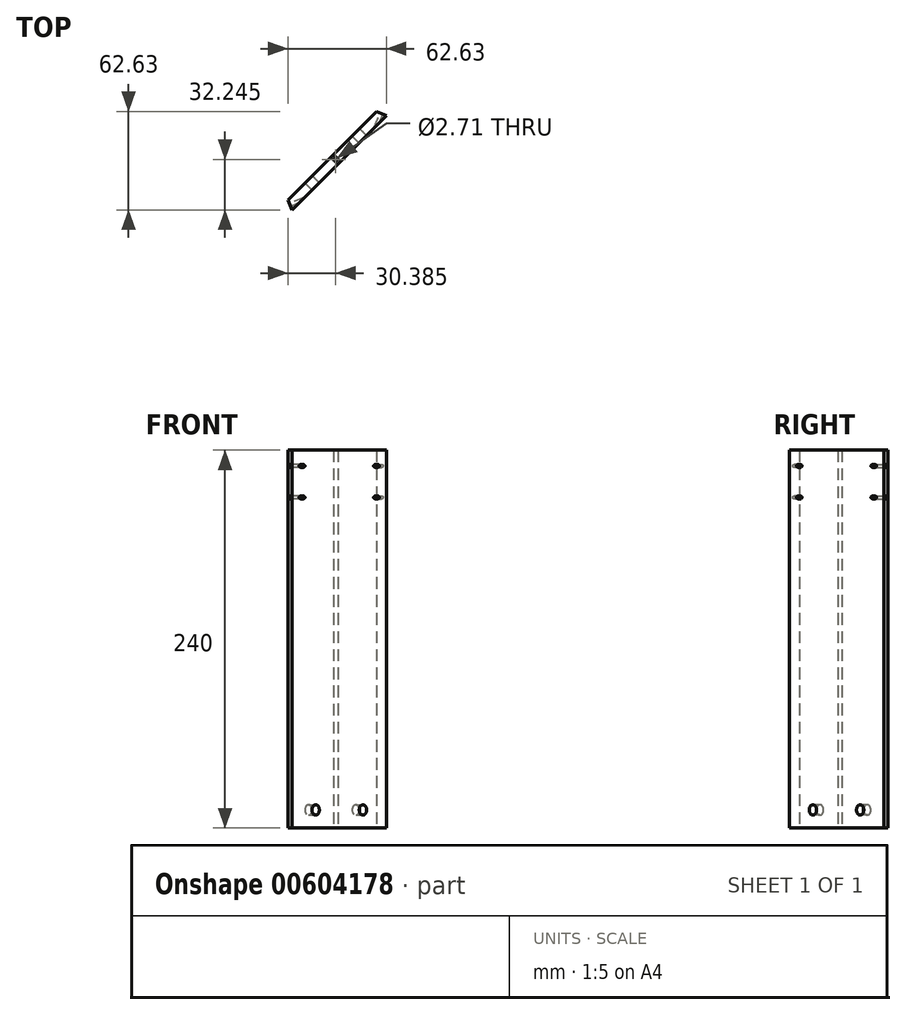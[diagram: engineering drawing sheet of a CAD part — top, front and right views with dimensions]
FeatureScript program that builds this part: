
annotation { "Feature Type Name" : "Feature", "Feature Type Description" : "" }
export const myFeature = defineFeature(function(context is Context, id is Id, definition is map)
    precondition{}
    {
        {
            var Q0;
            Q0=qCreatedBy(makeId("Top.planeOp"),FACE);
            var sketch = newSketch(context, id + "F0", { "sketchPlane" : qUnion([Q0])});
            skLineSegment(sketch, "E0", {"start": v(-120, 0) * mm, "end": v(-180, 60) * mm});
            skLineSegment(sketch, "E1", {"start": v(-180, 60) * mm, "end": v(-180, 220) * mm});
            skLineSegment(sketch, "E2", {"start": v(-180, 220) * mm, "end": v(-120, 280) * mm});
            skLineSegment(sketch, "E3", {"start": v(-120, 280) * mm, "end": v(120, 280) * mm});
            skLineSegment(sketch, "E4", {"start": v(120, 280) * mm, "end": v(180, 220) * mm});
            skLineSegment(sketch, "E5", {"start": v(180, 220) * mm, "end": v(180, 60) * mm});
            skLineSegment(sketch, "E6", {"start": v(180, 60) * mm, "end": v(120, 0) * mm});
            skLineSegment(sketch, "E7", {"start": v(120, 0) * mm, "end": v(-120, 0) * mm});
            skLineSegment(sketch, "E8.0", {"start": v(-173.65, 62.63) * mm, "end": v(-173.65, 217.37) * mm});
            skLineSegment(sketch, "E8.1", {"start": v(-117.37, 6.35) * mm, "end": v(-173.65, 62.63) * mm});
            skLineSegment(sketch, "E8.2", {"start": v(-173.65, 217.37) * mm, "end": v(-117.37, 273.65) * mm});
            skLineSegment(sketch, "E8.3", {"start": v(117.37, 6.35) * mm, "end": v(-117.37, 6.35) * mm});
            skLineSegment(sketch, "E8.4", {"start": v(-117.37, 273.65) * mm, "end": v(117.37, 273.65) * mm});
            skLineSegment(sketch, "E8.5", {"start": v(117.37, 273.65) * mm, "end": v(173.65, 217.37) * mm});
            skLineSegment(sketch, "E8.6", {"start": v(173.65, 217.37) * mm, "end": v(173.65, 62.63) * mm});
            skLineSegment(sketch, "E8.7", {"start": v(173.65, 62.63) * mm, "end": v(117.37, 6.35) * mm});
            skLineSegment(sketch, "E9", {"start": v(-120, 0) * mm, "end": v(-117.37, 6.35) * mm});
            skLineSegment(sketch, "E10", {"start": v(-120, 280) * mm, "end": v(-117.37, 273.65) * mm});
            skLineSegment(sketch, "E11", {"start": v(120, 280) * mm, "end": v(117.37, 273.65) * mm});
            skLineSegment(sketch, "E12", {"start": v(120, 0) * mm, "end": v(117.37, 6.35) * mm});
            skLineSegment(sketch, "E13", {"start": v(-173.65, 217.37) * mm, "end": v(-180, 220) * mm});
            skLineSegment(sketch, "E14", {"start": v(-173.65, 62.63) * mm, "end": v(-180, 60) * mm});
            skLineSegment(sketch, "E15", {"start": v(173.65, 62.63) * mm, "end": v(180, 60) * mm});
            skLineSegment(sketch, "E16", {"start": v(173.65, 217.37) * mm, "end": v(180, 220) * mm});
            skSolve(sketch);
        }
        {
            var Q0;
            Q0=makeQuery(id+"F0.imprint","IMPRINT",FACE,{"disambiguationData":[TD([[makeQuery(id+"F0.imprint","IMPRINT",EDGE,{"derivedFrom":sQuery(id+"F0.wireOp",EDGE,"E0")}),-1.0]])]});
            extrude(context, id + "F1", {"entities" : qUnion([Q0]), "depth" : 240 * mm, "offsetDistance" : 25 * mm});
        }
        {
            var Q0;
            Q0=makeQuery(id+"F0.imprint","IMPRINT",FACE,{"disambiguationData":[TD([[makeQuery(id+"F0.imprint","IMPRINT",EDGE,{"derivedFrom":sQuery(id+"F0.wireOp",EDGE,"E2")}),-1.0]])]});
            extrude(context, id + "F2", {"entities" : qUnion([Q0]), "depth" : 240 * mm, "offsetDistance" : 25 * mm});
        }
        {
            var Q0;
            Q0=makeQuery(id+"F0.imprint","IMPRINT",FACE,{"disambiguationData":[TD([[makeQuery(id+"F0.imprint","IMPRINT",EDGE,{"derivedFrom":sQuery(id+"F0.wireOp",EDGE,"E4")}),-1.0]])]});
            extrude(context, id + "F3", {"entities" : qUnion([Q0]), "depth" : 240 * mm, "offsetDistance" : 25 * mm});
        }
        {
            var Q0;
            Q0=makeQuery(id+"F0.imprint","IMPRINT",FACE,{"disambiguationData":[TD([[makeQuery(id+"F0.imprint","IMPRINT",EDGE,{"derivedFrom":sQuery(id+"F0.wireOp",EDGE,"E6")}),-1.0]])]});
            extrude(context, id + "F4", {"entities" : qUnion([Q0]), "depth" : 240 * mm, "offsetDistance" : 25 * mm});
        }
        {
            var Q0;
            Q0=makeQuery(id+"F1.opExtrude","SWEPT_FACE",FACE,{"disambiguationData":[OSD([sQuery(id+"F0.wireOp",EDGE,"E0")])]});
            var sketch = newSketch(context, id + "F5", { "sketchPlane" : qUnion([Q0])});
            skLineSegment(sketch, "E17", {"start": v(-169.7, 0) * mm, "end": v(-84.85, 0) * mm, "construction": true});
            skLineSegment(sketch, "E18", {"start": v(-84.85, 0) * mm, "end": v(-127.28, 0) * mm, "construction": true});
            skLineSegment(sketch, "E19", {"start": v(-127.28, 0) * mm, "end": v(-106.07, 0) * mm, "construction": true});
            skLineSegment(sketch, "E20", {"start": v(-106.07, 0) * mm, "end": v(-106.07, 11.51) * mm, "construction": true});
            skLineSegment(sketch, "E21", {"start": v(-127.28, 0) * mm, "end": v(-169.7, 0) * mm, "construction": true});
            skLineSegment(sketch, "E22", {"start": v(-148.5, 0) * mm, "end": v(-148.5, 11.51) * mm, "construction": true});
            skSolve(sketch);
        }
        {
            var Q0;
            Q0=makeQuery(id+"F4.opExtrude","SWEPT_FACE",FACE,{"disambiguationData":[OSD([sQuery(id+"F0.wireOp",EDGE,"E6")])]});
            var sketch = newSketch(context, id + "F6", { "sketchPlane" : qUnion([Q0])});
            skLineSegment(sketch, "E23", {"start": v(84.85, 0) * mm, "end": v(169.7, 0) * mm, "construction": true});
            skLineSegment(sketch, "E24", {"start": v(169.7, 0) * mm, "end": v(127.28, 0) * mm, "construction": true});
            skLineSegment(sketch, "E25", {"start": v(127.28, 0) * mm, "end": v(148.5, 0) * mm, "construction": true});
            skLineSegment(sketch, "E26", {"start": v(148.5, 0) * mm, "end": v(148.5, 11.51) * mm, "construction": true});
            skLineSegment(sketch, "E27", {"start": v(84.85, 0) * mm, "end": v(127.28, 0) * mm, "construction": true});
            skLineSegment(sketch, "E28", {"start": v(106.07, 0) * mm, "end": v(106.07, 11.51) * mm, "construction": true});
            skSolve(sketch);
        }
        {
            var Q0;
            Q0=makeQuery(id+"F3.opExtrude","SWEPT_FACE",FACE,{"disambiguationData":[OSD([sQuery(id+"F0.wireOp",EDGE,"E4")])]});
            var sketch = newSketch(context, id + "F7", { "sketchPlane" : qUnion([Q0])});
            skLineSegment(sketch, "E29", {"start": v(28.28, 0) * mm, "end": v(113.14, 0) * mm, "construction": true});
            skLineSegment(sketch, "E30", {"start": v(113.14, 0) * mm, "end": v(70.71, 0) * mm, "construction": true});
            skLineSegment(sketch, "E31", {"start": v(70.71, 0) * mm, "end": v(91.92, 0) * mm, "construction": true});
            skLineSegment(sketch, "E32", {"start": v(91.92, 0) * mm, "end": v(91.92, 11.51) * mm, "construction": true});
            skLineSegment(sketch, "E33", {"start": v(28.28, 0) * mm, "end": v(70.71, 0) * mm, "construction": true});
            skLineSegment(sketch, "E34", {"start": v(49.5, 0) * mm, "end": v(49.5, 11.51) * mm, "construction": true});
            skSolve(sketch);
        }
        {
            var Q0;
            Q0=makeQuery(id+"F2.opExtrude","SWEPT_FACE",FACE,{"disambiguationData":[OSD([sQuery(id+"F0.wireOp",EDGE,"E2")])]});
            var sketch = newSketch(context, id + "F8", { "sketchPlane" : qUnion([Q0])});
            skLineSegment(sketch, "E35", {"start": v(-113.14, 0) * mm, "end": v(-28.28, 0) * mm, "construction": true});
            skLineSegment(sketch, "E36", {"start": v(-28.28, 0) * mm, "end": v(-70.71, 0) * mm, "construction": true});
            skLineSegment(sketch, "E37", {"start": v(-70.71, 0) * mm, "end": v(-49.5, 0) * mm, "construction": true});
            skLineSegment(sketch, "E38", {"start": v(-49.5, 0) * mm, "end": v(-49.5, 11.51) * mm, "construction": true});
            skLineSegment(sketch, "E39", {"start": v(-113.14, 0) * mm, "end": v(-70.71, 0) * mm, "construction": true});
            skLineSegment(sketch, "E40", {"start": v(-91.92, 0) * mm, "end": v(-91.92, 11.51) * mm, "construction": true});
            skSolve(sketch);
        }
        {
            var Q0;
            Q0=sQuery(id+"F8.wireOp",VERTEX,"E40.end");
            var Q1;
            Q1=sQuery(id+"F8.wireOp",VERTEX,"E38.end");
            var Q2;
            Q2=sQuery(id+"F5.wireOp",VERTEX,"E20.end");
            var Q3;
            Q3=sQuery(id+"F5.wireOp",VERTEX,"E22.end");
            var Q4;
            Q4=sQuery(id+"F6.wireOp",VERTEX,"E26.end");
            var Q5;
            Q5=sQuery(id+"F6.wireOp",VERTEX,"E28.end");
            var Q6;
            Q6=sQuery(id+"F7.wireOp",VERTEX,"E34.end");
            var Q7;
            Q7=sQuery(id+"F7.wireOp",VERTEX,"E32.end");
            var Q8;
            Q8=makeQuery(id+"F2.opExtrude","SWEPT_BODY",BODY,{"disambiguationData":[OSD([sQuery(id+"F0.wireOp",EDGE,"E2"),sQuery(id+"F0.wireOp",EDGE,"E8.2"),sQuery(id+"F0.wireOp",EDGE,"E10"),sQuery(id+"F0.wireOp",EDGE,"E13")])]});
            var Q9;
            Q9=makeQuery(id+"F1.opExtrude","SWEPT_BODY",BODY,{"disambiguationData":[OSD([sQuery(id+"F0.wireOp",EDGE,"E0"),sQuery(id+"F0.wireOp",EDGE,"E8.1"),sQuery(id+"F0.wireOp",EDGE,"E9"),sQuery(id+"F0.wireOp",EDGE,"E14")])]});
            var Q10;
            Q10=makeQuery(id+"F4.opExtrude","SWEPT_BODY",BODY,{"disambiguationData":[OSD([sQuery(id+"F0.wireOp",EDGE,"E6"),sQuery(id+"F0.wireOp",EDGE,"E8.7"),sQuery(id+"F0.wireOp",EDGE,"E12"),sQuery(id+"F0.wireOp",EDGE,"E15")])]});
            var Q11;
            Q11=makeQuery(id+"F3.opExtrude","SWEPT_BODY",BODY,{"disambiguationData":[OSD([sQuery(id+"F0.wireOp",EDGE,"E4"),sQuery(id+"F0.wireOp",EDGE,"E8.5"),sQuery(id+"F0.wireOp",EDGE,"E11"),sQuery(id+"F0.wireOp",EDGE,"E16")])]});
            hole(context, id + "F9", {"style" : HoleStyle.SIMPLE, "endStyle" : HoleEndStyle.BLIND, "standardTappedOrClearance" : lookupTablePath({ "standard" : "ISO", "fit" : "Normal", "size" : "M6", "type" : "Clearance" }), "standardBlindInLast" : lookupTablePath({ "fit" : "Standard", "standard" : "ISO", "size" : "M6", "type" : "Clearance" }), "holeDiameter" : 6.6 * mm, "majorDiameter" : 5 * mm, "holeDepth" : 12 * mm, "isTappedThrough" : true, "tappedDepth" : 12 * mm, "tapClearance" : 3, "locations" : qUnion([Q0, Q1, Q2, Q3, Q4, Q5, Q6, Q7]), "scope" : qUnion([Q8, Q9, Q10, Q11])});
        }
        {
            var Q0;
            Q0=makeQuery(id+"F1.opExtrude","CAP_FACE",FACE,{"disambiguationData":[OSD([sQuery(id+"F0.wireOp",EDGE,"E0"),sQuery(id+"F0.wireOp",EDGE,"E8.1"),sQuery(id+"F0.wireOp",EDGE,"E9"),sQuery(id+"F0.wireOp",EDGE,"E14")])],"isStart":true});
            var sketch = newSketch(context, id + "F10", { "sketchPlane" : qUnion([Q0])});
            skLineSegment(sketch, "E41", {"start": v(-150, -30) * mm, "end": v(-147.75, -32.25) * mm, "construction": true});
            skSolve(sketch);
        }
        {
            var Q0;
            Q0=makeQuery(id+"F4.opExtrude","CAP_FACE",FACE,{"disambiguationData":[OSD([sQuery(id+"F0.wireOp",EDGE,"E6"),sQuery(id+"F0.wireOp",EDGE,"E8.7"),sQuery(id+"F0.wireOp",EDGE,"E12"),sQuery(id+"F0.wireOp",EDGE,"E15")])],"isStart":true});
            var sketch = newSketch(context, id + "F11", { "sketchPlane" : qUnion([Q0])});
            skLineSegment(sketch, "E42", {"start": v(150, -30) * mm, "end": v(147.75, -32.25) * mm, "construction": true});
            skSolve(sketch);
        }
        {
            var Q0;
            Q0=makeQuery(id+"F2.opExtrude","CAP_FACE",FACE,{"disambiguationData":[OSD([sQuery(id+"F0.wireOp",EDGE,"E2"),sQuery(id+"F0.wireOp",EDGE,"E8.2"),sQuery(id+"F0.wireOp",EDGE,"E10"),sQuery(id+"F0.wireOp",EDGE,"E13")])],"isStart":true});
            var sketch = newSketch(context, id + "F12", { "sketchPlane" : qUnion([Q0])});
            skLineSegment(sketch, "E43", {"start": v(-150, -250) * mm, "end": v(-147.75, -247.75) * mm, "construction": true});
            skSolve(sketch);
        }
        {
            var Q0;
            Q0=sQuery(id+"F11.wireOp",VERTEX,"E42.end");
            var Q1;
            Q1=sQuery(id+"F10.wireOp",VERTEX,"E41.end");
            var Q2;
            Q2=sQuery(id+"F12.wireOp",VERTEX,"E43.end");
            var Q3;
            Q3=makeQuery(id+"F1.opExtrude","SWEPT_BODY",BODY,{"disambiguationData":[OSD([sQuery(id+"F0.wireOp",EDGE,"E0"),sQuery(id+"F0.wireOp",EDGE,"E8.1"),sQuery(id+"F0.wireOp",EDGE,"E9"),sQuery(id+"F0.wireOp",EDGE,"E14")])]});
            var Q4;
            Q4=makeQuery(id+"F2.opExtrude","SWEPT_BODY",BODY,{"disambiguationData":[OSD([sQuery(id+"F0.wireOp",EDGE,"E2"),sQuery(id+"F0.wireOp",EDGE,"E8.2"),sQuery(id+"F0.wireOp",EDGE,"E10"),sQuery(id+"F0.wireOp",EDGE,"E13")])]});
            var Q5;
            Q5=makeQuery(id+"F3.opExtrude","SWEPT_BODY",BODY,{"disambiguationData":[OSD([sQuery(id+"F0.wireOp",EDGE,"E4"),sQuery(id+"F0.wireOp",EDGE,"E8.5"),sQuery(id+"F0.wireOp",EDGE,"E11"),sQuery(id+"F0.wireOp",EDGE,"E16")])]});
            var Q6;
            Q6=makeQuery(id+"F4.opExtrude","SWEPT_BODY",BODY,{"disambiguationData":[OSD([sQuery(id+"F0.wireOp",EDGE,"E6"),sQuery(id+"F0.wireOp",EDGE,"E8.7"),sQuery(id+"F0.wireOp",EDGE,"E12"),sQuery(id+"F0.wireOp",EDGE,"E15")])]});
            hole(context, id + "F13", {"style" : HoleStyle.SIMPLE, "endStyle" : HoleEndStyle.THROUGH, "standardTappedOrClearance" : lookupTablePath({ "standard" : "ANSI", "engagement" : "75%", "pitch" : "32 tpi", "size" : "#6", "type" : "Tapped" }), "standardBlindInLast" : lookupTablePath({ "standard" : "ANSI", "engagement" : "75%", "pitch" : "32 tpi", "size" : "#6", "type" : "Tapped" }), "holeDiameter" : 2.7 * mm, "majorDiameter" : 3.5 * mm, "showTappedDepth" : true, "isTappedThrough" : true, "tappedDepth" : 12 * mm, "tapClearance" : 3, "locations" : qUnion([Q0, Q1, Q2]), "scope" : qUnion([Q3, Q4, Q5, Q6])});
        }
        {
            var Q0;
            Q0=makeQuery(id+"F4.opExtrude","SWEPT_FACE",FACE,{"disambiguationData":[OSD([sQuery(id+"F0.wireOp",EDGE,"E12")])]});
            var sketch = newSketch(context, id + "F14", { "sketchPlane" : qUnion([Q0])});
            skLineSegment(sketch, "E44", {"start": v(42.49, 240) * mm, "end": v(42.49, 230) * mm, "construction": true});
            skLineSegment(sketch, "E45", {"start": v(42.49, 230) * mm, "end": v(42.49, 210) * mm, "construction": true});
            skSolve(sketch);
        }
        {
            var Q0;
            Q0=makeQuery(id+"F4.opExtrude","SWEPT_FACE",FACE,{"disambiguationData":[OSD([sQuery(id+"F0.wireOp",EDGE,"E15")])]});
            var sketch = newSketch(context, id + "F15", { "sketchPlane" : qUnion([Q0])});
            skLineSegment(sketch, "E46", {"start": v(-139.9, 240) * mm, "end": v(-139.9, 230) * mm, "construction": true});
            skLineSegment(sketch, "E47", {"start": v(-139.9, 230) * mm, "end": v(-139.9, 210) * mm, "construction": true});
            skSolve(sketch);
        }
        {
            var Q0;
            Q0=makeQuery(id+"F3.opExtrude","SWEPT_BODY",BODY,{"disambiguationData":[OSD([sQuery(id+"F0.wireOp",EDGE,"E4"),sQuery(id+"F0.wireOp",EDGE,"E8.5"),sQuery(id+"F0.wireOp",EDGE,"E11"),sQuery(id+"F0.wireOp",EDGE,"E16")])]});
            var Q1;
            Q1=makeQuery(id+"F2.opExtrude","SWEPT_BODY",BODY,{"disambiguationData":[OSD([sQuery(id+"F0.wireOp",EDGE,"E2"),sQuery(id+"F0.wireOp",EDGE,"E8.2"),sQuery(id+"F0.wireOp",EDGE,"E10"),sQuery(id+"F0.wireOp",EDGE,"E13")])]});
            var Q2;
            Q2=makeQuery(id+"F1.opExtrude","SWEPT_BODY",BODY,{"disambiguationData":[OSD([sQuery(id+"F0.wireOp",EDGE,"E0"),sQuery(id+"F0.wireOp",EDGE,"E8.1"),sQuery(id+"F0.wireOp",EDGE,"E9"),sQuery(id+"F0.wireOp",EDGE,"E14")])]});
            deleteBodies(context, id + "F16", {"entities" : qUnion([Q0, Q1, Q2])});
        }
        {
            var Q0;
            Q0=sQuery(id+"F15.wireOp",VERTEX,"E47.start");
            var Q1;
            Q1=sQuery(id+"F15.wireOp",VERTEX,"E47.end");
            var Q2;
            Q2=sQuery(id+"F14.wireOp",VERTEX,"E44.end");
            var Q3;
            Q3=sQuery(id+"F14.wireOp",VERTEX,"E45.end");
            var Q4;
            Q4=makeQuery(id+"F4.opExtrude","SWEPT_BODY",BODY,{"disambiguationData":[OSD([sQuery(id+"F0.wireOp",EDGE,"E6"),sQuery(id+"F0.wireOp",EDGE,"E8.7"),sQuery(id+"F0.wireOp",EDGE,"E12"),sQuery(id+"F0.wireOp",EDGE,"E15")])]});
            hole(context, id + "F17", {"style" : HoleStyle.SIMPLE, "endStyle" : HoleEndStyle.THROUGH, "standardTappedOrClearance" : lookupTablePath({ "standard" : "ANSI", "engagement" : "75%", "pitch" : "48 tpi", "size" : "#3", "type" : "Tapped" }), "standardBlindInLast" : lookupTablePath({ "standard" : "ANSI", "engagement" : "75%", "pitch" : "48 tpi", "size" : "#3", "type" : "Tapped" }), "holeDiameter" : 2 * mm, "majorDiameter" : 2.5 * mm, "showTappedDepth" : true, "isTappedThrough" : true, "tappedDepth" : 12 * mm, "tapClearance" : 3, "locations" : qUnion([Q0, Q1, Q2, Q3]), "scope" : qUnion([Q4])});
        }
    });
